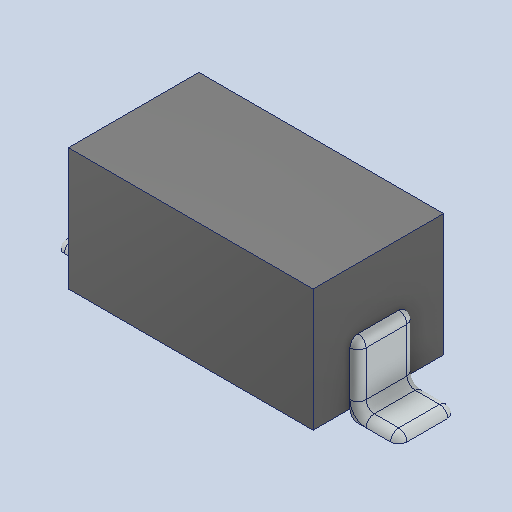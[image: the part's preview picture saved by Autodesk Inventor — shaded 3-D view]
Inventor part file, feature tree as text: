
AUTODESK INVENTOR PART (.ipt)
format: ipt  version: 2024 (Build 280153000, 153)  size: 134,656 bytes
history: native  units: in
note: dims shown in document units (in); Inventor stores cm internally (conversion verified against a paired STEP export)
features: mirror x1
ambient origin geometry x8: Origin, YZ Plane, XZ Plane, XY Plane, X Axis, Y Axis, Z Axis, Center Point
bodies: Solid1 (feature_tree)
feature tree (1):
  mirror  "Mirror1"
